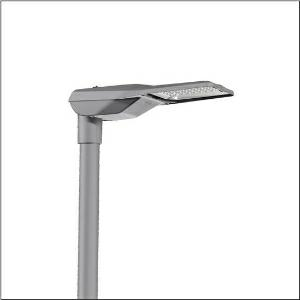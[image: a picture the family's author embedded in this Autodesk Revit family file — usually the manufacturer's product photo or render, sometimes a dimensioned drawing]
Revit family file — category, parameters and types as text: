
# Revit family: streetlight_sl_21_mini___st0_8a_5xe2c43s08hb_a304
name_source: partatom
category: Lighting Fixtures
units: mm (PartAtom-declared; Revit-internal decimal feet)

## family parameters
Cut with Voids When Loaded = No
Host = Face
Light Source = No
Part Type = Normal
Room Calculation Point = No
Round Connector Dimension = Use Diameter
Shared = No

## types (1)
- --- (1 x LED, 9430 lm, 66 W, 4000K)
    Apparent Load = 66 VA
    CIE Flux Codes = 38 75 97 100 100
    Color Rendering = 70
    Color Temperature = 4000K
    Default Elevation = 1800 mm
    Description = Streetlight SL 21 mini, mast luminaire, primary light control with lens, of PMMA, primary optical cover: cover, of toughened safety glass, transparent, light distribution: ST0.8a, light emission: direct distribution, primary light characteristic: asymmetric, installation type: side-entry, post-top, LED, High Power LED, rated luminous flux: 9.430lm, luminous efficacy: 143lm/W, light colour: 740, colour temperature: 4000K, control gear: D4i, control: overheat protection, constant luminous flux control, time-dependent luminous flux control, flexible luminous flux parameterisation, pre-setting: logarithmic dimming characteristic, mains connection: 220..240V, AC, 50/60Hz, start of lifetime: 66W, end of service life: 69W, reduction: 30W, luminaire housing, of diecast aluminium, powder-coated, SITECO metallic grey (DB 702S), corrosivity category C5 high according to DIN EN ISO 12944, please order mast flange separately, inclination adjustable: 0°, 5°, 10°, 15°, sealing non-destructively replaceable, multi-level sealing system, length: 628mm, width: 235mm, height: 110mm, mast flange for spigot size: 42mm (side-entry): 5XC10008XM4, 60/48mm (side-entry/post-top): 5XC10108XM2, 76/60mm (side-entry/post-top): 5XC10108XM1, mounting height: 4..8m, Smart Interface above, protection rating (complete): IP66, insulation class (complete): insulation class II (safety insulation), certification: CE, ENEC, ENEC+, VDE, impact resistance: IK10, permissible operating ambient temperature for outdoor applications: -40..+50°C, standard-compliant lighting for roads and squares, packaging unit: 1 piece

Light Distribution: ST0.8a
    Height = 110 mm
    Lamp = 1 x LED
    Lamp Light Flux = 9430 lm
    Lamp Power = 66 W
    Lamp count = 1
    Length = 625 mm
    Luminous efficacy = 143 lm/W
    Manufacturer = Siteco
    ModVariant = No
    Model = 5XE2C43S08HB
    Number of Poles = 1
    OnlyDefault = Yes
    Power Factor = 1
    Product Name = Streetlight SL 21 mini | ST0.8a
    Product group = mast luminaire | pylon top
    ProductGroupID = 6100
    Protection Class = Protection class II
    Protection Degree = IP 66
    RLX_Detail_Level = 1
    RLX_Emergency_Light_Flux = 0 lm
    RLX_Emergency_Type = 0
    RLX_Emergency_Type_DB = No
    RlxData = <blob elided: 26165 chars, md5=06b4e059>
    Socket = socket
    Standby Power = 0 W
    System Light Flux = 9430 lm
    System Power = 66 W
    Type Comments = factory setting: luminous flux: 100 % | dim-lin: 254 | 670 mA
    Type Image = l_1003515.jpg
    URL = http://relux.com
    VarID = @adj_182919
    Voltage = 0 V
    Weight = 0.00 kg
    Width = 234 mm

## geometry (parser evidence)
native form markers: Blend x4, Sweep x12
no freeform markers — native parametric forms only
